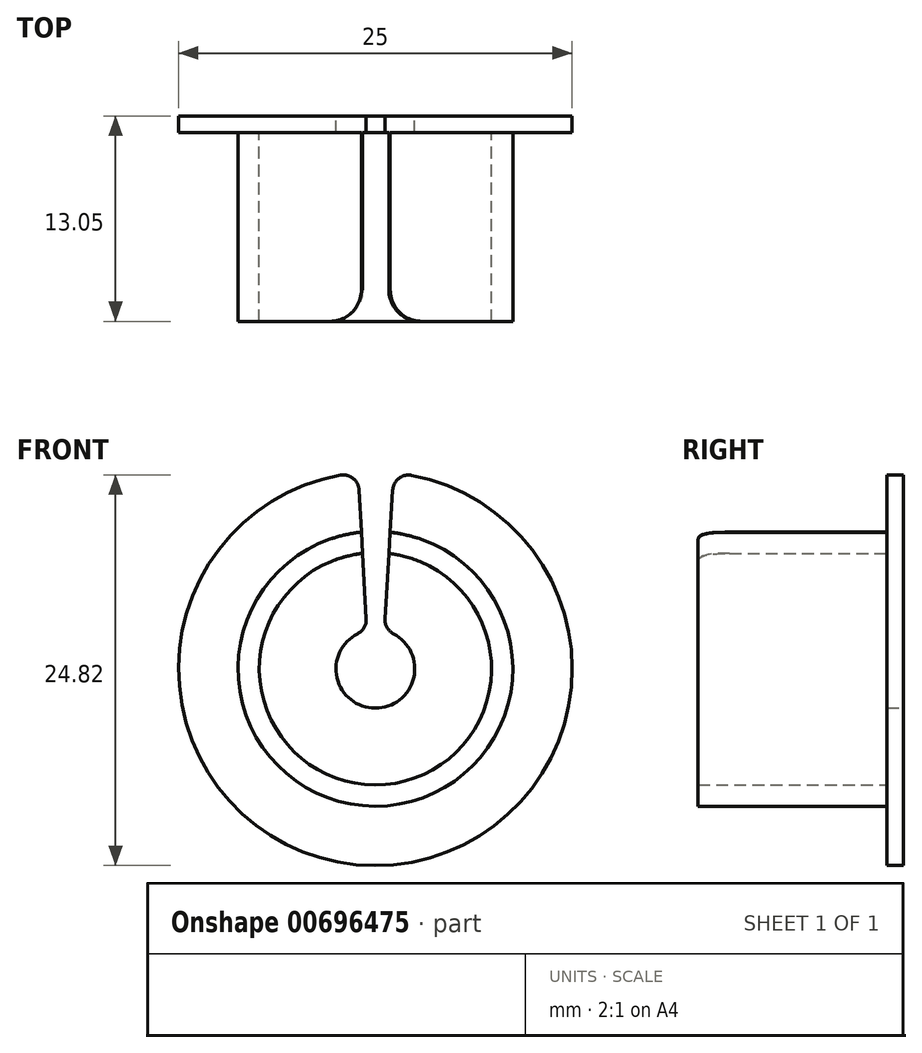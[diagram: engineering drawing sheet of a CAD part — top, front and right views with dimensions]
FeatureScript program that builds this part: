
annotation { "Feature Type Name" : "Feature", "Feature Type Description" : "" }
export const myFeature = defineFeature(function(context is Context, id is Id, definition is map)
    precondition{}
    {
        {
            var Q0;
            Q0=qCreatedBy(makeId("Front.planeOp"),FACE);
            var sketch = newSketch(context, id + "F0", { "sketchPlane" : qUnion([Q0])});
            skCircle(sketch, "E0", {"center": v(0, 0) * mm, "radius": 12.5 * mm});
            skCircle(sketch, "E1", {"center": v(0, 0) * mm, "radius": 2.5 * mm});
            skLineSegment(sketch, "E2", {"start": v(-1.1, 12.45) * mm, "end": v(-0.54, 2.44) * mm});
            skLineSegment(sketch, "E3", {"start": v(1.17, 12.45) * mm, "end": v(0.57, 2.43) * mm});
            skSolve(sketch);
        }
        {
            var Q0;
            {var subQ0=sQuery(id+"F0.wireOp",EDGE,"E2");Q0=makeQuery(id+"F0.imprint","IMPRINT",FACE,{"disambiguationData":[TD([[makeQuery(id+"F0.imprint","IMPRINT",EDGE,{"derivedFrom":subQ0}),-1.0]])]});}
            extrude(context, id + "F1", {"entities" : qUnion([Q0]), "depth" : 1.05 * mm, "offsetDistance" : 25 * mm});
        }
        {
            var Q0;
            Q0=makeQuery(id+"F1.opExtrude","SWEPT_EDGE",EDGE,{"disambiguationData":[OSD([sQuery(id+"F0.wireOp",EDGE,"E0"),sQuery(id+"F0.wireOp",EDGE,"E2")])]});
            var Q1;
            Q1=makeQuery(id+"F1.opExtrude","SWEPT_EDGE",EDGE,{"disambiguationData":[OSD([sQuery(id+"F0.wireOp",EDGE,"E0"),sQuery(id+"F0.wireOp",EDGE,"E3")])]});
            var Q2;
            Q2=makeQuery(id+"F1.opExtrude","SWEPT_EDGE",EDGE,{"disambiguationData":[OSD([sQuery(id+"F0.wireOp",EDGE,"E1"),sQuery(id+"F0.wireOp",EDGE,"E2")])]});
            var Q3;
            Q3=makeQuery(id+"F1.opExtrude","SWEPT_EDGE",EDGE,{"disambiguationData":[OSD([sQuery(id+"F0.wireOp",EDGE,"E1"),sQuery(id+"F0.wireOp",EDGE,"E3")])]});
            fillet(context, id + "F2", {"entities" : qUnion([Q0, Q1, Q2, Q3]), "radius" : 1 * mm, "tangentPropagation" : true, "allowEdgeOverflow" : false});
        }
        {
            var Q0;
            Q0=makeQuery(id+"F1.opExtrude","CAP_FACE",FACE,{"disambiguationData":[OSD([sQuery(id+"F0.wireOp",EDGE,"E0"),sQuery(id+"F0.wireOp",EDGE,"E1"),sQuery(id+"F0.wireOp",EDGE,"E2"),sQuery(id+"F0.wireOp",EDGE,"E3")])],"isStart":false});
            var sketch = newSketch(context, id + "F3", { "sketchPlane" : qUnion([Q0])});
            skCircle(sketch, "E4", {"center": v(0, 0) * mm, "radius": 7.38 * mm});
            skCircle(sketch, "E5.0", {"center": v(0, 0) * mm, "radius": 8.72 * mm});
            skLineSegment(sketch, "E6", {"start": v(-0.9, 8.68) * mm, "end": v(-0.82, 7.33) * mm});
            skLineSegment(sketch, "E7", {"start": v(0.94, 8.67) * mm, "end": v(0.86, 7.32) * mm});
            skSolve(sketch);
        }
        {
            var Q0;
            {var subQ0=sQuery(id+"F3.wireOp",EDGE,"E6");Q0=makeQuery(id+"F3.imprint","IMPRINT",FACE,{"disambiguationData":[TD([[makeQuery(id+"F3.imprint","IMPRINT",EDGE,{"derivedFrom":subQ0}),-1.0]])]});}
            extrude(context, id + "F4", {"entities" : qUnion([Q0]), "operationType" : NewBodyOperationType.ADD, "depth" : 12 * mm, "offsetDistance" : 25 * mm});
        }
        {
            var Q0;
            Q0=makeQuery(id+"F4.opExtrude","CAP_EDGE",EDGE,{"disambiguationData":[OSD([sQuery(id+"F3.wireOp",EDGE,"E6")])],"isStart":false});
            var Q1;
            Q1=makeQuery(id+"F4.opExtrude","CAP_EDGE",EDGE,{"disambiguationData":[OSD([sQuery(id+"F3.wireOp",EDGE,"E7")])],"isStart":false});
            fillet(context, id + "F5", {"entities" : qUnion([Q0, Q1]), "radius" : 2 * mm, "tangentPropagation" : true, "allowEdgeOverflow" : false});
        }
    });
